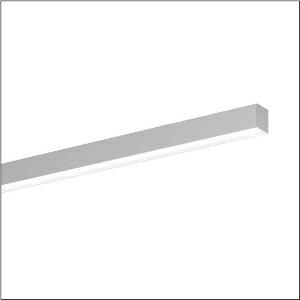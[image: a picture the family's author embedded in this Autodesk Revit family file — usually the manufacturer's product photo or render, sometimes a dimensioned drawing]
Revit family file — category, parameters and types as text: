
# Revit family: silica_r__21_51mx20tat2s_7558
name_source: partatom
category: Lighting Fixtures
units: mm (PartAtom-declared; Revit-internal decimal feet)

## family parameters
Cut with Voids When Loaded = No
Host = Face
Light Source = No
Part Type = Normal
Room Calculation Point = No
Round Connector Dimension = Use Diameter
Shared = No

## types (1)
- --- (1 x LED, 2400 lm, 20.5 W, 6500K)
    Apparent Load = 21 VA
    CIE Flux Codes = 48 79 96 100 100
    Color Rendering = 80
    Color Temperature = 6500K
    Default Elevation = 1800 mm
    Description = Silica® 21, office luminaire, primary optical cover: cover, of PMMA, opal, light emission: direct distribution, primary light characteristic: symmetric, installation type: surface-mounted, LED, rated luminous flux: 2.400lm, luminous efficacy: 112lm/W, light colour: 8tw, colour temperature: 2700..6500K, control gear: ECG DALI, with terminal, 3+2-pole, max. 2.5mm², mains connection: 220..240V, AC, 50/60Hz, rated input power: 21.5W, luminaire housing, of aluminium, metallic grey (RAL 9006), length: 1.204mm, width: 53mm, height: 53mm, protection rating (complete): IP20, insulation class (complete): insulation class I (protective earthing), certification: CE, permissible operating ambient temperature: 0..+35°C, standard: EN 50419, packaging unit: 1 piece
    Height = 0 mm  [stored 0 ft]
    Lamp = 1 x LED
    Lamp Light Flux = 2400 lm
    Lamp Power = 20.5 W
    Lamp count = 1
    Length = 1204 mm
    Luminous efficacy = 117 lm/W
    Manufacturer = Siteco
    ModVariant = No
    Model = 51MX20TAT2S
    Mounting Place = Ceiling
    Mounting Type = Recessed
    Number of Poles = 1
    OnlyDefault = Yes
    Power Factor = 1
    Product Name = Silica® 21
    Product group = office luminaire | ceiling recessed
    ProductGroupID = 401
    Protection Class = Protection class I
    Protection Degree = IP 20
    RLX_Detail_Level = 1
    RLX_Emergency_Light_Flux = 0 lm
    RLX_Emergency_Type = 0
    RLX_Emergency_Type_DB = No
    RlxData = <blob elided: 23201 chars, md5=3ad8063a>
    Socket = socket
    Standby Power = 0 W
    System Light Flux = 2400 lm
    System Power = 21 W
    Type Comments = individual setting
    Type Image = l_1297768.jpg
    URL = http://relux.com
    VarID = @adj_070999
    Voltage = 0 V
    Weight = 0.00 kg
    Width = 53 mm

note: [stored X ft] marks values corroborated as IEEE doubles in the binary element streams (Revit-internal decimal feet)

## geometry (parser evidence)
native form markers: Blend x4, Sweep x12
no freeform markers — native parametric forms only
